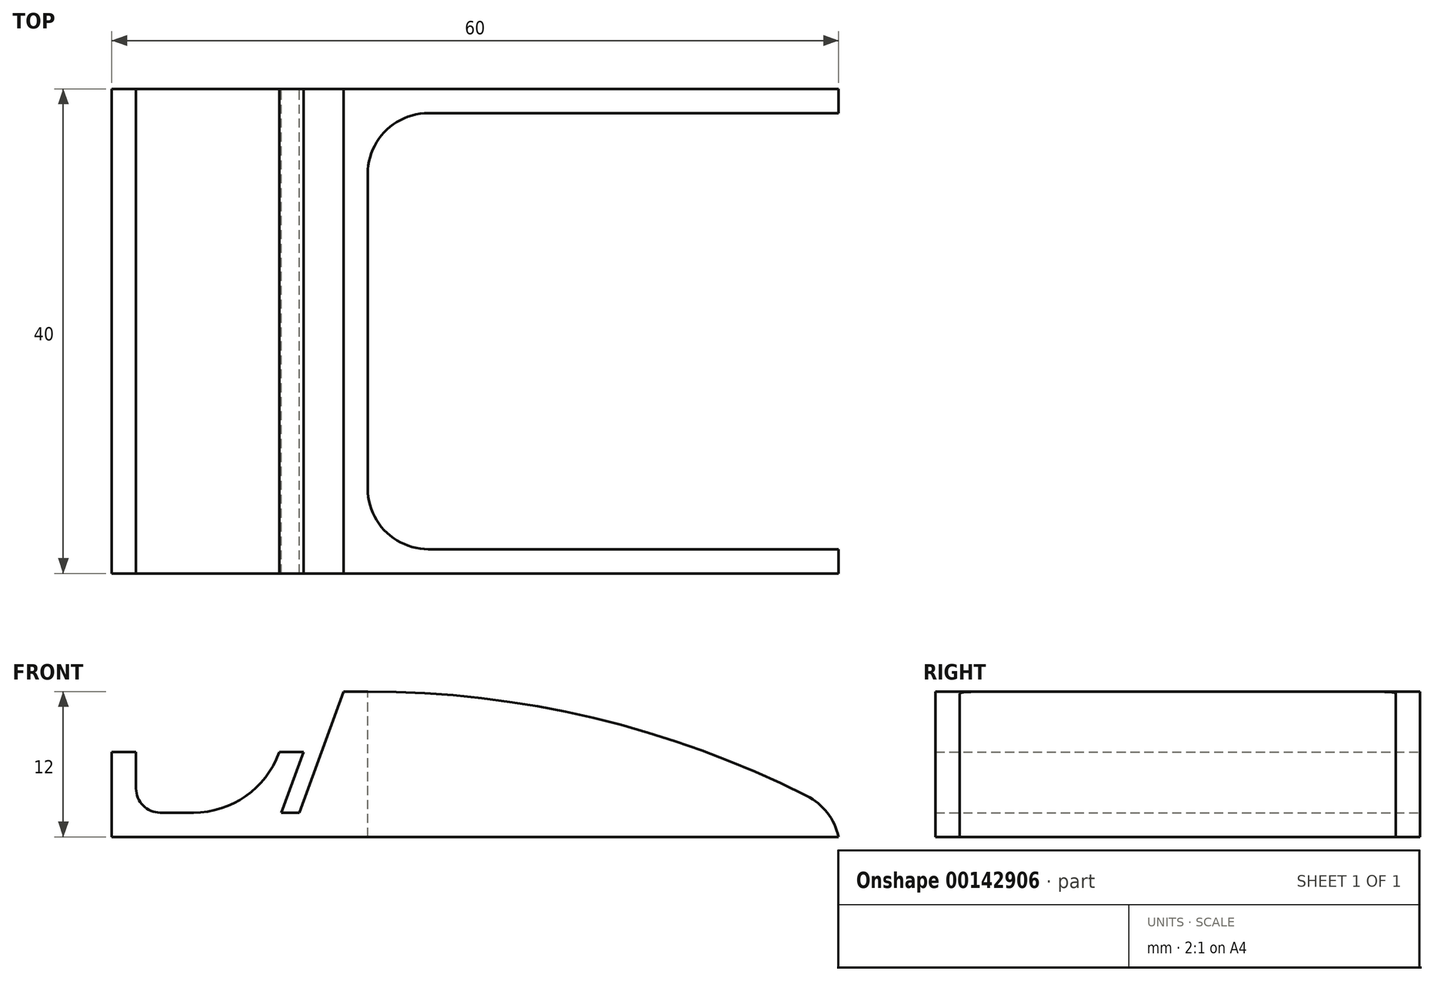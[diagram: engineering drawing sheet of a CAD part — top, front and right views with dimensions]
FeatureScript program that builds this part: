
annotation { "Feature Type Name" : "Feature", "Feature Type Description" : "" }
export const myFeature = defineFeature(function(context is Context, id is Id, definition is map)
    precondition{}
    {
        {
            var Q0;
            Q0=qCreatedBy(makeId("Front.planeOp"),FACE);
            var sketch = newSketch(context, id + "F0", { "sketchPlane" : qUnion([Q0])});
            skLineSegment(sketch, "E0", {"start": v(-58, 0) * mm, "end": v(-58, 5) * mm});
            skLineSegment(sketch, "E1", {"start": v(-58, 5) * mm, "end": v(-60, 5) * mm});
            skLineSegment(sketch, "E2", {"start": v(-60, 5) * mm, "end": v(-60, -2) * mm});
            skLineSegment(sketch, "E3", {"start": v(-60, -2) * mm, "end": v(0, -2) * mm});
            skLineSegment(sketch, "E4", {"start": v(0, -2) * mm, "end": v(0, 0) * mm});
            skLineSegment(sketch, "E5", {"start": v(-38.87, 10) * mm, "end": v(-40.87, 10) * mm});
            skLineSegment(sketch, "E6", {"start": v(-40.87, 10) * mm, "end": v(-44.51, 0) * mm});
            skLineSegment(sketch, "E7", {"start": v(-44.51, 0) * mm, "end": v(-46, 0) * mm});
            skLineSegment(sketch, "E8", {"start": v(-46, 0) * mm, "end": v(-44.18, 5) * mm});
            skLineSegment(sketch, "E9", {"start": v(-44.18, 5) * mm, "end": v(-46.18, 5) * mm});
            skLineSegment(sketch, "E10", {"start": v(-46.18, 5) * mm, "end": v(-48, 0) * mm});
            skLineSegment(sketch, "E11", {"start": v(-48, 0) * mm, "end": v(-58, 0) * mm});
            skArc(sketch, "E12", {"start": v(0, 0) * mm, "mid": v(-18.8, 7.46) * mm, "end": v(-38.87, 10) * mm});
            skSolve(sketch);
        }
        {
            var Q0;
            Q0=makeQuery(id+"F0.imprint","IMPRINT",FACE,{"disambiguationData":[TD([[makeQuery(id+"F0.imprint","IMPRINT",EDGE,{"derivedFrom":sQuery(id+"F0.wireOp",EDGE,"E0")}),1.0]])]});
            extrude(context, id + "F1", {"entities" : qUnion([Q0]), "depth" : 40 * mm});
        }
        {
            var Q0;
            Q0=makeQuery(id+"F1.opExtrude","SWEPT_FACE",FACE,{"disambiguationData":[OSD([sQuery(id+"F0.wireOp",EDGE,"E5")])]});
            var sketch = newSketch(context, id + "F2", { "sketchPlane" : qUnion([Q0])});
            skLineSegment(sketch, "E13.bottom", {"start": v(-38.87, -2) * mm, "end": v(0, -2) * mm});
            skLineSegment(sketch, "E13.top", {"start": v(-38.87, -38) * mm, "end": v(0, -38) * mm});
            skLineSegment(sketch, "E13.left", {"start": v(-38.87, -2) * mm, "end": v(-38.87, -38) * mm});
            skLineSegment(sketch, "E13.right", {"start": v(0, -2) * mm, "end": v(0, -38) * mm});
            skSolve(sketch);
        }
        {
            var Q0;
            Q0=makeQuery(id+"F2.imprint","IMPRINT",FACE,{"disambiguationData":[TD([[makeQuery(id+"F2.imprint","IMPRINT",EDGE,{"derivedFrom":sQuery(id+"F2.wireOp",EDGE,"E13.bottom")}),-1.0]])]});
            extrude(context, id + "F3", {"entities" : qUnion([Q0]), "operationType" : NewBodyOperationType.REMOVE, "oppositeDirection" : true, "depth" : 25 * mm});
        }
        {
            var Q0;
            Q0=makeQuery(id+"F1.opExtrude","SWEPT_EDGE",EDGE,{"disambiguationData":[OSD([sQuery(id+"F0.wireOp",EDGE,"E10"),sQuery(id+"F0.wireOp",EDGE,"E11")])]});
            fillet(context, id + "F4", {"entities" : qUnion([Q0]), "radius" : 7.5 * mm, "tangentPropagation" : true, "allowEdgeOverflow" : false});
        }
        {
            var Q0;
            Q0=makeQuery(id+"F1.opExtrude","SWEPT_EDGE",EDGE,{"disambiguationData":[OSD([sQuery(id+"F0.wireOp",EDGE,"E0"),sQuery(id+"F0.wireOp",EDGE,"E11")])]});
            fillet(context, id + "F5", {"entities" : qUnion([Q0]), "radius" : 2 * mm, "tangentPropagation" : true, "allowEdgeOverflow" : false});
        }
        {
            var Q0;
            {var subQ0=sQuery(id+"F0.wireOp",EDGE,"E12");var subQ1=sQuery(id+"F0.wireOp",EDGE,"E4");Q0=makeQuery(id+"F3.boolean.opBoolean","SPLIT",EDGE,{"disambiguationData":[TD([makeQuery(id+"F3.opExtrude","SWEPT_FACE",FACE,{"disambiguationData":[OSD([sQuery(id+"F2.wireOp",EDGE,"E13.top")])]})])],"derivedFrom":makeQuery(id+"F1.opExtrude","SWEPT_EDGE",EDGE,{"disambiguationData":[OSD([subQ1,subQ0])]})});}
            var Q1;
            {var subQ0=sQuery(id+"F0.wireOp",EDGE,"E12");var subQ1=sQuery(id+"F0.wireOp",EDGE,"E4");Q1=makeQuery(id+"F3.boolean.opBoolean","SPLIT",EDGE,{"disambiguationData":[TD([makeQuery(id+"F3.opExtrude","SWEPT_FACE",FACE,{"disambiguationData":[OSD([sQuery(id+"F2.wireOp",EDGE,"E13.bottom")])]})])],"derivedFrom":makeQuery(id+"F1.opExtrude","SWEPT_EDGE",EDGE,{"disambiguationData":[OSD([subQ1,subQ0])]})});}
            fillet(context, id + "F6", {"entities" : qUnion([Q0, Q1]), "radius" : 5 * mm, "tangentPropagation" : true, "allowEdgeOverflow" : false});
        }
        {
            var Q0;
            Q0=makeQuery(id+"F3.boolean.opBoolean","COPY",EDGE,{"derivedFrom":makeQuery(id+"F3.opExtrude","SWEPT_EDGE",EDGE,{"disambiguationData":[OSD([sQuery(id+"F0.wireOp",EDGE,"E5"),sQuery(id+"F0.wireOp",EDGE,"E12"),sQuery(id+"F2.wireOp",EDGE,"E13.top"),sQuery(id+"F2.wireOp",EDGE,"E13.left")])]})});
            var Q1;
            Q1=makeQuery(id+"F3.boolean.opBoolean","COPY",EDGE,{"derivedFrom":makeQuery(id+"F3.opExtrude","SWEPT_EDGE",EDGE,{"disambiguationData":[OSD([sQuery(id+"F0.wireOp",EDGE,"E5"),sQuery(id+"F0.wireOp",EDGE,"E12"),sQuery(id+"F2.wireOp",EDGE,"E13.bottom"),sQuery(id+"F2.wireOp",EDGE,"E13.left")])]})});
            fillet(context, id + "F7", {"entities" : qUnion([Q0, Q1]), "radius" : 5 * mm, "tangentPropagation" : true, "allowEdgeOverflow" : false});
        }
    });
